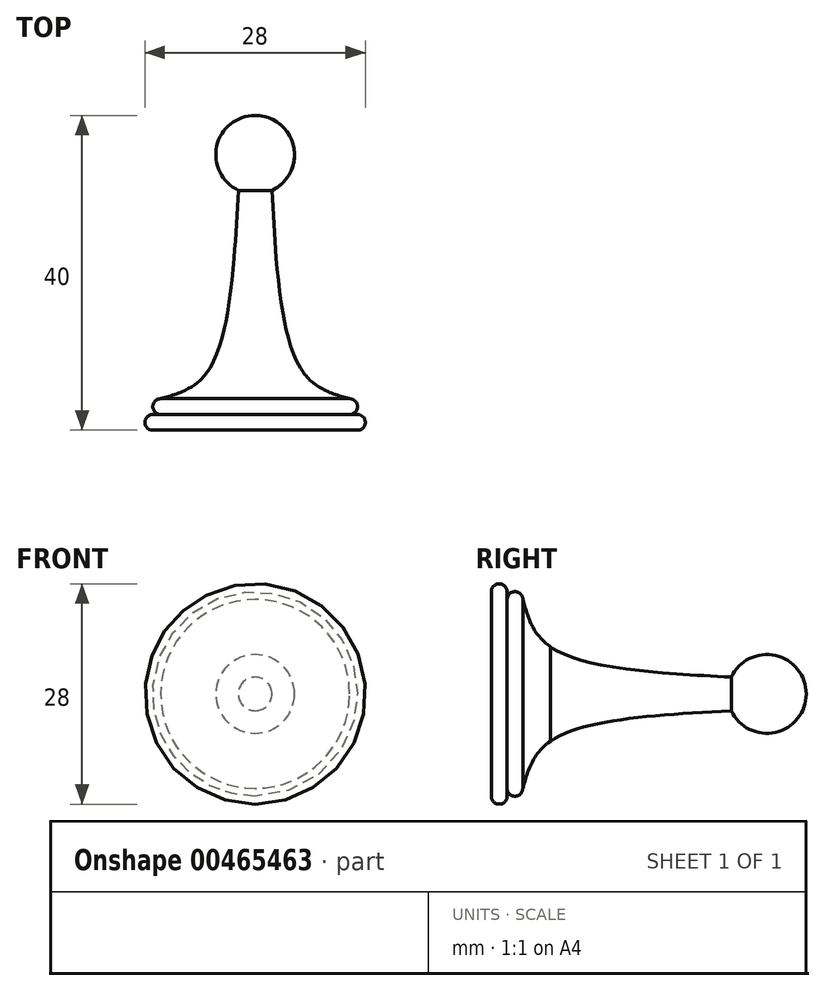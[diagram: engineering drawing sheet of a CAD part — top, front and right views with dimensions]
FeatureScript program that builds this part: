
annotation { "Feature Type Name" : "Feature", "Feature Type Description" : "" }
export const myFeature = defineFeature(function(context is Context, id is Id, definition is map)
    precondition{}
    {
        {
            var Q0;
            Q0=qCreatedBy(makeId("Top.planeOp"),FACE);
            var sketch = newSketch(context, id + "F0", { "sketchPlane" : qUnion([Q0])});
            skLineSegment(sketch, "E0", {"start": v(0, 0) * mm, "end": v(13, 0) * mm});
            skLineSegment(sketch, "E1", {"start": v(13, 0) * mm, "end": v(13, 1) * mm});
            skCircle(sketch, "E2", {"center": v(13, 1) * mm, "radius": 1 * mm});
            skLineSegment(sketch, "E3", {"start": v(13, 1) * mm, "end": v(13, 2) * mm});
            skLineSegment(sketch, "E4", {"start": v(13, 2) * mm, "end": v(12, 2) * mm});
            skLineSegment(sketch, "E5", {"start": v(12, 2) * mm, "end": v(12, 3) * mm});
            skArc(sketch, "E6", {"start": v(12, 2) * mm, "mid": v(13, 3) * mm, "end": v(12, 4) * mm});
            skLineSegment(sketch, "E7", {"start": v(12, 3) * mm, "end": v(12, 4) * mm});
            skPoint(sketch, "E8.end.orphan", {"position": v(0, 20) * mm});
            skPoint(sketch, "E9.end.orphan", {"position": v(0, 40) * mm});
            skLineSegment(sketch, "E10", {"start": v(0, 0) * mm, "end": v(0, 15) * mm});
            skLineSegment(sketch, "E11", {"start": v(0, 15) * mm, "end": v(0, 40) * mm});
            skLineSegment(sketch, "E12", {"start": v(0, 15) * mm, "end": v(0, 35) * mm});
            skArc(sketch, "E13", {"start": v(2.13, 30.48) * mm, "mid": v(4.88, 36.1) * mm, "end": v(0, 40) * mm});
            skLineSegment(sketch, "E14", {"start": v(0, 0) * mm, "end": v(0, 7.5) * mm});
            skLineSegment(sketch, "E15", {"start": v(0, 7.5) * mm, "end": v(6, 7.5) * mm});
            skFitSpline(sketch, "E16", {"points": [v(12, 4) * mm, v(6, 7.5) * mm, v(2.13, 30.48) * mm], "startDerivative": vector(-18.93, 5.39) * mm, "endDerivative": vector(-2.42, 43.8) * mm});
            skSolve(sketch);
        }
        {
            var Q0;
            {var subQ1=sQuery(id+"F0.wireOp",EDGE,"E0");Q0=makeQuery(id+"F0.imprint","IMPRINT",FACE,{"disambiguationData":[TD([[makeQuery(id+"F0.imprint","IMPRINT",EDGE,{"derivedFrom":subQ1}),1.0]])]});}
            var Q1;
            Q1=makeQuery(id+"F0.imprint","IMPRINT",FACE,{"disambiguationData":[TD([[makeQuery(id+"F0.imprint","IMPRINT",EDGE,{"derivedFrom":sQuery(id+"F0.wireOp",EDGE,"E5")}),-1.0]])]});
            var Q2;
            {var subQ0=sQuery(id+"F0.wireOp",EDGE,"E1");Q2=makeQuery(id+"F0.imprint","IMPRINT",FACE,{"disambiguationData":[TD([[makeQuery(id+"F0.imprint","IMPRINT",EDGE,{"derivedFrom":subQ0}),-1.0]])]});}
            var Q3;
            {var subQ0=sQuery(id+"F0.wireOp",EDGE,"E1");Q3=makeQuery(id+"F0.imprint","IMPRINT",FACE,{"disambiguationData":[TD([[makeQuery(id+"F0.imprint","IMPRINT",EDGE,{"derivedFrom":subQ0}),1.0]])]});}
            var Q4;
            Q4=makeQuery(id+"F0.imprint","IMPRINT",FACE,{"disambiguationData":[TD([[makeQuery(id+"F0.imprint","IMPRINT",EDGE,{"derivedFrom":sQuery(id+"F0.wireOp",EDGE,"E10")}),-1.0]])]});
            var Q5;
            Q5=sQuery(id+"F0.wireOp",EDGE,"E12");
            revolve(context, id + "F1", {"entities" : qUnion([Q0, Q1, Q2, Q3, Q4]), "axis" : qUnion([Q5]), "revolveType" : RevolveType.FULL});
        }
    });
